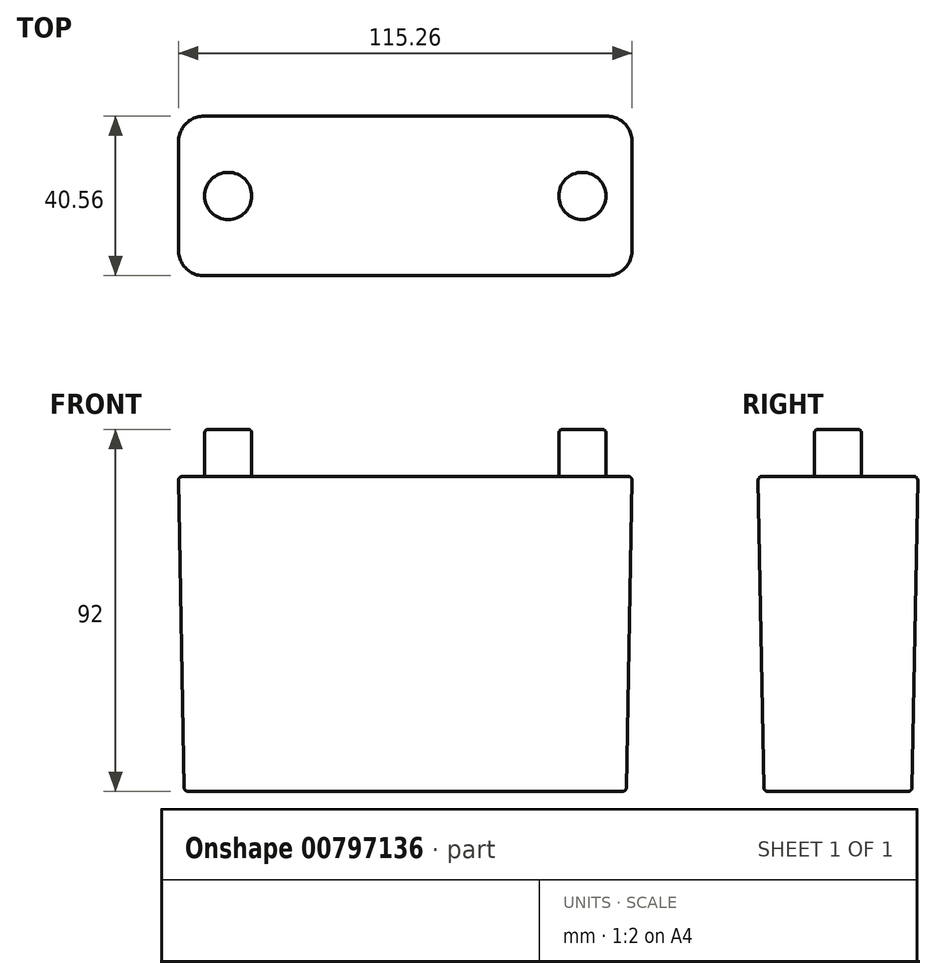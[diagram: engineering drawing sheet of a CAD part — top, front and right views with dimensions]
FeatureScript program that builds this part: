
annotation { "Feature Type Name" : "Feature", "Feature Type Description" : "" }
export const myFeature = defineFeature(function(context is Context, id is Id, definition is map)
    precondition{}
    {
        {
            var Q0;
            Q0=qCreatedBy(makeId("Top.planeOp"),FACE);
            var sketch = newSketch(context, id + "F0", { "sketchPlane" : qUnion([Q0])});
            skLineSegment(sketch, "E0.bottom", {"start": v(51.15, -18.8) * mm, "end": v(-51.15, -18.8) * mm});
            skLineSegment(sketch, "E0.top", {"start": v(51.15, 18.8) * mm, "end": v(-51.15, 18.8) * mm});
            skLineSegment(sketch, "E0.left", {"start": v(56.15, -13.8) * mm, "end": v(56.15, 13.8) * mm});
            skLineSegment(sketch, "E0.right", {"start": v(-56.15, -13.8) * mm, "end": v(-56.15, 13.8) * mm});
            skPoint(sketch, "E0.middle", {"position": v(0, 0) * mm});
            skPoint(sketch, "E1.visualSharp", {"position": v(-56.15, 18.8) * mm});
            skArc(sketch, "E1.filletArc", {"start": v(-51.15, 18.8) * mm, "mid": v(-54.69, 17.34) * mm, "end": v(-56.15, 13.8) * mm});
            skPoint(sketch, "E2.visualSharp", {"position": v(56.15, 18.8) * mm});
            skArc(sketch, "E2.filletArc", {"start": v(56.15, 13.8) * mm, "mid": v(54.69, 17.34) * mm, "end": v(51.15, 18.8) * mm});
            skPoint(sketch, "E3.visualSharp", {"position": v(56.15, -18.8) * mm});
            skArc(sketch, "E3.filletArc", {"start": v(51.15, -18.8) * mm, "mid": v(54.69, -17.34) * mm, "end": v(56.15, -13.8) * mm});
            skPoint(sketch, "E4.visualSharp", {"position": v(-56.15, -18.8) * mm});
            skArc(sketch, "E4.filletArc", {"start": v(-56.15, -13.8) * mm, "mid": v(-54.69, -17.34) * mm, "end": v(-51.15, -18.8) * mm});
            skSolve(sketch);
        }
        {
            var Q0;
            Q0=qCreatedBy(makeId("Top.planeOp"),FACE);
            cPlane(context, id + "F1", {"entities" : qUnion([Q0]), "cplaneType" : CPlaneType.OFFSET, "offset" : 80 * mm, "width" : 150 * mm, "height" : 150 * mm});
        }
        {
            var Q0;
            Q0=qCreatedBy(id+"F1.planeOp",FACE);
            var sketch = newSketch(context, id + "F2", { "sketchPlane" : qUnion([Q0])});
            skLineSegment(sketch, "E5.0", {"start": v(51.15, 20.3) * mm, "end": v(-51.15, 20.3) * mm});
            skArc(sketch, "E5.1", {"start": v(57.65, 13.8) * mm, "mid": v(55.75, 18.4) * mm, "end": v(51.15, 20.3) * mm});
            skArc(sketch, "E5.2", {"start": v(-51.15, 20.3) * mm, "mid": v(-55.75, 18.4) * mm, "end": v(-57.65, 13.8) * mm});
            skLineSegment(sketch, "E5.3", {"start": v(57.65, -13.8) * mm, "end": v(57.65, 13.8) * mm});
            skLineSegment(sketch, "E5.4", {"start": v(-57.65, -13.8) * mm, "end": v(-57.65, 13.8) * mm});
            skArc(sketch, "E5.5", {"start": v(-57.65, -13.8) * mm, "mid": v(-55.75, -18.4) * mm, "end": v(-51.15, -20.3) * mm});
            skLineSegment(sketch, "E5.6", {"start": v(51.15, -20.3) * mm, "end": v(-51.15, -20.3) * mm});
            skArc(sketch, "E5.7", {"start": v(51.15, -20.3) * mm, "mid": v(55.75, -18.4) * mm, "end": v(57.65, -13.8) * mm});
            skSolve(sketch);
        }
        {
            var Q0;
            Q0 = qSketchRegion(id + "F0", true);
            var Q1;
            Q1 = qSketchRegion(id + "F2", true);
            loft(context, id + "F3", {"sheetProfilesArray" : [{ "sheetProfileEntities" : qUnion([Q0]) }, { "sheetProfileEntities" : qUnion([Q1]) }]});
        }
        {
            var Q0;
            Q0=makeQuery(id+"F3.opLoft","CAP_FACE",FACE,{"disambiguationData":[OSD([makeQuery(id+"F2.imprint","IMPRINT",FACE,{"disambiguationData":[TD([[makeQuery(id+"F2.imprint","IMPRINT",EDGE,{"derivedFrom":sQuery(id+"F2.wireOp",EDGE,"E5.0")}),1.0]])]})])],"isStart":true});
            var sketch = newSketch(context, id + "F4", { "sketchPlane" : qUnion([Q0])});
            skCircle(sketch, "E6", {"center": v(-45, 0) * mm, "radius": 6 * mm});
            skCircle(sketch, "E7", {"center": v(45, 0) * mm, "radius": 6 * mm});
            skSolve(sketch);
        }
        {
            var Q0;
            Q0 = qSketchRegion(id + "F4", true);
            extrude(context, id + "F5", {"entities" : qUnion([Q0]), "operationType" : NewBodyOperationType.ADD, "depth" : 12 * mm, "offsetDistance" : 25 * mm});
        }
        {
            var Q0;
            Q0=makeQuery(id+"F5.opExtrude","CAP_EDGE",EDGE,{"disambiguationData":[OSD([sQuery(id+"F4.wireOp",EDGE,"E6")])],"isStart":false});
            var Q1;
            Q1=makeQuery(id+"F5.opExtrude","CAP_EDGE",EDGE,{"disambiguationData":[OSD([sQuery(id+"F4.wireOp",EDGE,"E7")])],"isStart":false});
            fillet(context, id + "F6", {"entities" : qUnion([Q0, Q1]), "radius" : 1 * mm, "tangentPropagation" : true, "allowEdgeOverflow" : false});
        }
        {
            var Q0;
            Q0=makeQuery(id+"F3.opLoft","MID_CAP_EDGE",EDGE,{"disambiguationData":[OSD([sQuery(id+"F2.wireOp",EDGE,"E5.2"),sQuery(id+"F2.wireOp",EDGE,"E5.4"),sQuery(id+"F2.wireOp",EDGE,"E5.5")])],"capPos":1.0});
            var Q1;
            Q1=makeQuery(id+"F3.opLoft","MID_CAP_EDGE",EDGE,{"disambiguationData":[OSD([sQuery(id+"F0.wireOp",EDGE,"E0.bottom"),sQuery(id+"F0.wireOp",EDGE,"E3.filletArc"),sQuery(id+"F0.wireOp",EDGE,"E4.filletArc")])],"capPos":0.0});
            fillet(context, id + "F7", {"entities" : qUnion([Q0, Q1]), "radius" : 1 * mm, "tangentPropagation" : true, "allowEdgeOverflow" : false});
        }
    });
